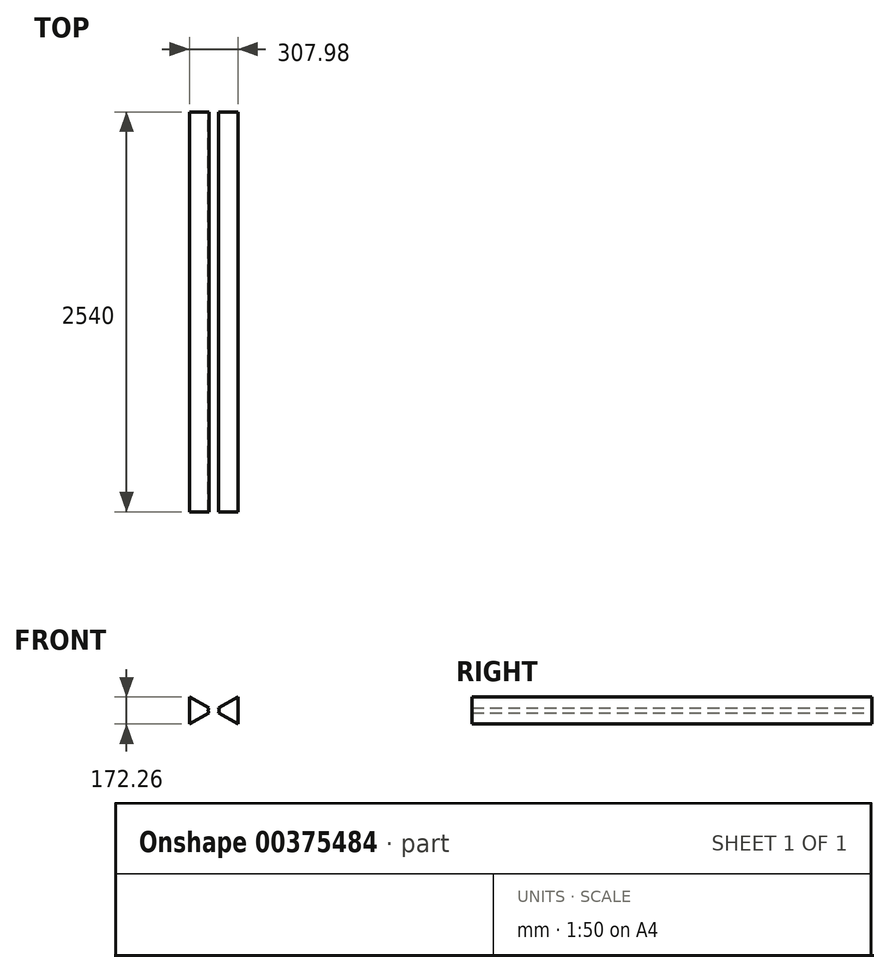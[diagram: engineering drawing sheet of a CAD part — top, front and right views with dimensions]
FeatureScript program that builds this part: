
annotation { "Feature Type Name" : "Feature", "Feature Type Description" : "" }
export const myFeature = defineFeature(function(context is Context, id is Id, definition is map)
    precondition{}
    {
        {
            var Q0;
            Q0=qCreatedBy(makeId("Front.planeOp"),FACE);
            var sketch = newSketch(context, id + "F0", { "sketchPlane" : qUnion([Q0])});
            skLineSegment(sketch, "E0", {"start": v(-154, 86.46) * mm, "end": v(154, -85.8) * mm});
            skLineSegment(sketch, "E1", {"start": v(154, 85.9) * mm, "end": v(-154, -85.8) * mm});
            skLineSegment(sketch, "E2", {"start": v(-154, 86.46) * mm, "end": v(-154, -85.8) * mm});
            skLineSegment(sketch, "E3", {"start": v(154, 85.9) * mm, "end": v(154, -85.8) * mm});
            skCircle(sketch, "E4", {"center": v(0, 0) * mm, "radius": 34.61 * mm});
            skSolve(sketch);
        }
        {
            var Q0;
            {var subQ0=sQuery(id+"F0.wireOp",EDGE,"E3");Q0=makeQuery(id+"F0.imprint","IMPRINT",FACE,{"disambiguationData":[TD([[makeQuery(id+"F0.imprint","IMPRINT",EDGE,{"derivedFrom":subQ0}),-1.0]])]});}
            var Q1;
            {var subQ0=sQuery(id+"F0.wireOp",EDGE,"E4");var subQ1=sQuery(id+"F0.wireOp",EDGE,"E0");var subQ2=makeQuery(id+"F0.imprint","INTERSECT",VERTEX,{"disambiguationData":[OD(0.0)],"derivedFrom":[subQ1,subQ0]});Q1=makeQuery(id+"F0.imprint","IMPRINT",FACE,{"disambiguationData":[TD([[makeQuery(id+"F0.imprint","IMPRINT",EDGE,{"disambiguationData":[TD([[subQ2,-1.0]])],"derivedFrom":subQ1}),1.0]])]});}
            var Q2;
            {var subQ0=sQuery(id+"F0.wireOp",EDGE,"E4");var subQ1=sQuery(id+"F0.wireOp",EDGE,"E0");var subQ2=makeQuery(id+"F0.imprint","INTERSECT",VERTEX,{"disambiguationData":[OD(1.0)],"derivedFrom":[subQ1,subQ0]});Q2=makeQuery(id+"F0.imprint","IMPRINT",FACE,{"disambiguationData":[TD([[makeQuery(id+"F0.imprint","IMPRINT",EDGE,{"disambiguationData":[TD([[subQ2,1.0]])],"derivedFrom":subQ1}),-1.0]])]});}
            var Q3;
            {var subQ0=sQuery(id+"F0.wireOp",EDGE,"E4");var subQ1=sQuery(id+"F0.wireOp",EDGE,"E0");var subQ2=makeQuery(id+"F0.imprint","INTERSECT",VERTEX,{"disambiguationData":[OD(0.0)],"derivedFrom":[subQ1,subQ0]});Q3=makeQuery(id+"F0.imprint","IMPRINT",FACE,{"disambiguationData":[TD([[makeQuery(id+"F0.imprint","IMPRINT",EDGE,{"disambiguationData":[TD([[subQ2,-1.0]])],"derivedFrom":subQ1}),-1.0]])]});}
            var Q4;
            {var subQ0=sQuery(id+"F0.wireOp",EDGE,"E4");var subQ1=sQuery(id+"F0.wireOp",EDGE,"E0");var subQ2=makeQuery(id+"F0.imprint","INTERSECT",VERTEX,{"disambiguationData":[OD(1.0)],"derivedFrom":[subQ1,subQ0]});Q4=makeQuery(id+"F0.imprint","IMPRINT",FACE,{"disambiguationData":[TD([[makeQuery(id+"F0.imprint","IMPRINT",EDGE,{"disambiguationData":[TD([[subQ2,1.0]])],"derivedFrom":subQ1}),1.0]])]});}
            var Q5;
            {var subQ0=sQuery(id+"F0.wireOp",EDGE,"E2");Q5=makeQuery(id+"F0.imprint","IMPRINT",FACE,{"disambiguationData":[TD([[makeQuery(id+"F0.imprint","IMPRINT",EDGE,{"derivedFrom":subQ0}),1.0]])]});}
            extrude(context, id + "F1", {"entities" : qUnion([Q0, Q1, Q2, Q3, Q4, Q5]), "depth" : 2540 * mm});
        }
    });
